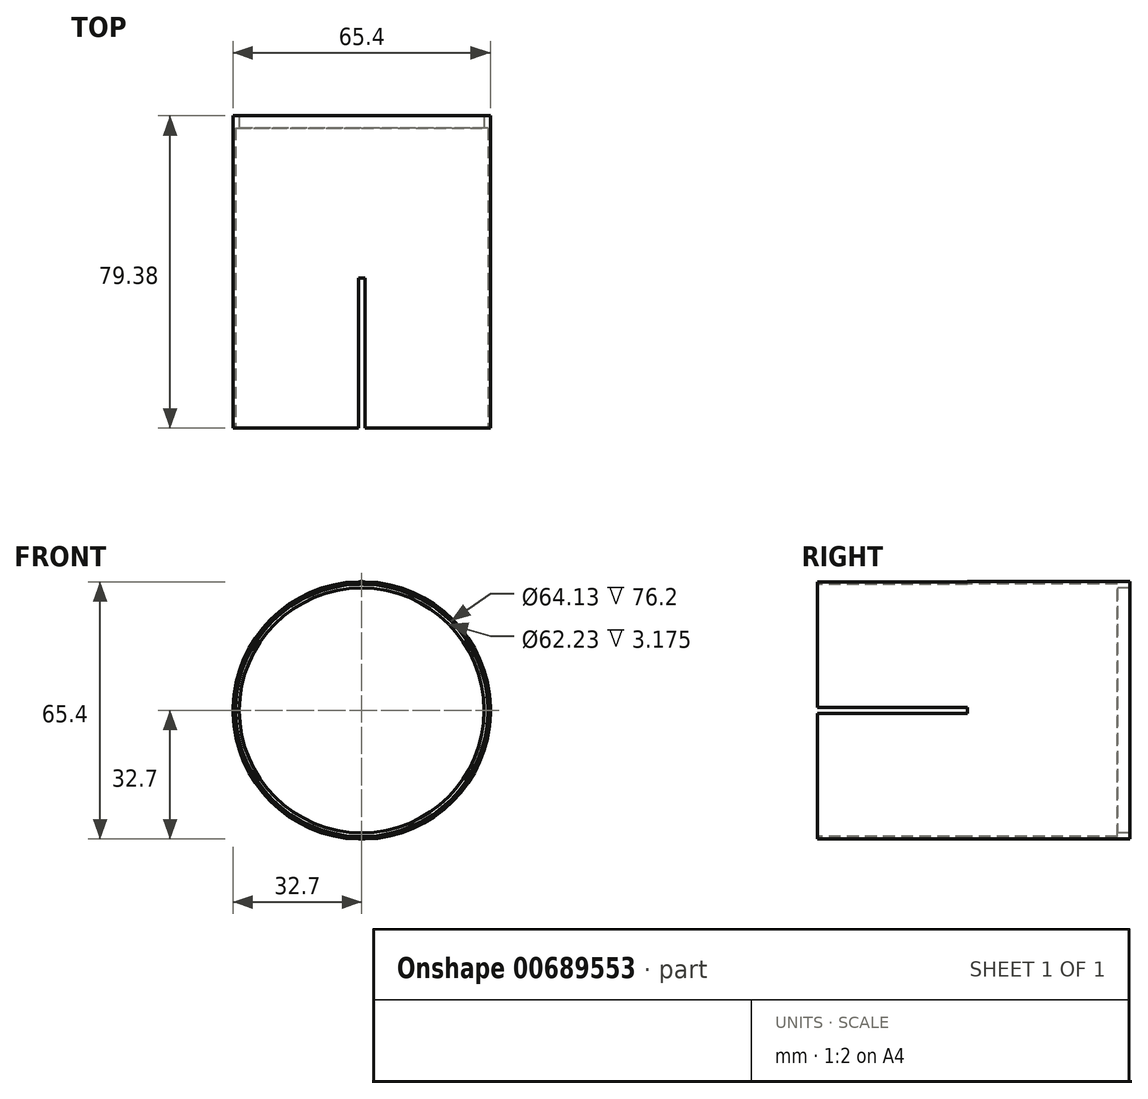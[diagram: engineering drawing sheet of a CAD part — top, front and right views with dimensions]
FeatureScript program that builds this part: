
annotation { "Feature Type Name" : "Feature", "Feature Type Description" : "" }
export const myFeature = defineFeature(function(context is Context, id is Id, definition is map)
    precondition{}
    {
        {
            var Q0;
            Q0=qCreatedBy(makeId("Front.planeOp"),FACE);
            var sketch = newSketch(context, id + "F0", { "sketchPlane" : qUnion([Q0])});
            skCircle(sketch, "E0", {"center": v(0, 0) * mm, "radius": 32.7 * mm});
            skCircle(sketch, "E1", {"center": v(0, 0) * mm, "radius": 32.07 * mm});
            skSolve(sketch);
        }
        {
            var Q0;
            Q0 = qSketchRegion(id + "F0", true);
            extrude(context, id + "F1", {"entities" : qUnion([Q0]), "oppositeDirection" : true, "depth" : 76.2 * mm, "offsetDistance" : 25.4 * mm});
        }
        {
            var Q0;
            Q0=qCreatedBy(makeId("Front.planeOp"),FACE);
            var sketch = newSketch(context, id + "F2", { "sketchPlane" : qUnion([Q0])});
            skLineSegment(sketch, "E2", {"start": v(0.8, 51.37) * mm, "end": v(-0.8, 51.37) * mm});
            skLineSegment(sketch, "E3", {"start": v(-0.8, 51.37) * mm, "end": v(-0.8, 0.8) * mm});
            skLineSegment(sketch, "E4", {"start": v(-0.8, -42.45) * mm, "end": v(0.8, -42.45) * mm});
            skLineSegment(sketch, "E5", {"start": v(0.8, -42.45) * mm, "end": v(0.8, -0.8) * mm});
            skLineSegment(sketch, "E6", {"start": v(50.8, -0.8) * mm, "end": v(50.8, 0.8) * mm});
            skLineSegment(sketch, "E7", {"start": v(50.8, 0.8) * mm, "end": v(0.8, 0.8) * mm});
            skLineSegment(sketch, "E8", {"start": v(-50.8, 0.8) * mm, "end": v(-50.8, -0.8) * mm});
            skLineSegment(sketch, "E9", {"start": v(-50.8, -0.8) * mm, "end": v(-0.8, -0.8) * mm});
            skLineSegment(sketch, "E10.trimOffspring", {"start": v(-0.8, -0.8) * mm, "end": v(-0.8, -42.45) * mm});
            skLineSegment(sketch, "E11.trimOffspring", {"start": v(-0.8, 0.8) * mm, "end": v(-50.8, 0.8) * mm});
            skLineSegment(sketch, "E12.trimOffspring", {"start": v(0.8, 0.8) * mm, "end": v(0.8, 51.37) * mm});
            skLineSegment(sketch, "E13.trimOffspring", {"start": v(0.8, -0.8) * mm, "end": v(50.8, -0.8) * mm});
            skSolve(sketch);
        }
        {
            var Q0;
            Q0 = qSketchRegion(id + "F2", true);
            extrude(context, id + "F3", {"entities" : qUnion([Q0]), "operationType" : NewBodyOperationType.REMOVE, "oppositeDirection" : true, "depth" : 38.1 * mm, "offsetDistance" : 25.4 * mm});
        }
        {
            var Q0;
            Q0=makeQuery(id+"F1.opExtrude","CAP_FACE",FACE,{"disambiguationData":[OSD([sQuery(id+"F0.wireOp",EDGE,"E0"),sQuery(id+"F0.wireOp",EDGE,"E1")])],"isStart":false});
            var sketch = newSketch(context, id + "F4", { "sketchPlane" : qUnion([Q0])});
            skCircle(sketch, "E14", {"center": v(0, 0) * mm, "radius": 32.7 * mm});
            skCircle(sketch, "E15", {"center": v(0, 0) * mm, "radius": 31.12 * mm});
            skSolve(sketch);
        }
        {
            var Q0;
            Q0 = qSketchRegion(id + "F4", true);
            extrude(context, id + "F5", {"entities" : qUnion([Q0]), "operationType" : NewBodyOperationType.ADD, "depth" : 3.17 * mm, "offsetDistance" : 25.4 * mm});
        }
    });
